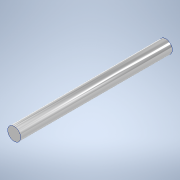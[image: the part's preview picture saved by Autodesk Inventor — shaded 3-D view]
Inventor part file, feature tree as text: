
AUTODESK INVENTOR PART (.ipt)
format: ipt  version: 2020.3 (Build 243373000, 373)  size: 96,768 bytes
history: native  units: mm
features: other x1, extrude x1, sketch x1
ambient origin geometry x8: Origin, YZ Plane, XZ Plane, XY Plane, X Axis, Y Axis, Z Axis, Center Point
bodies: Body1 (feature_tree)
feature tree (3):
  other  "ソリッド1"
  extrude  "押し出し1"  Depth=6.0mm
  sketch  "スケッチ1"
